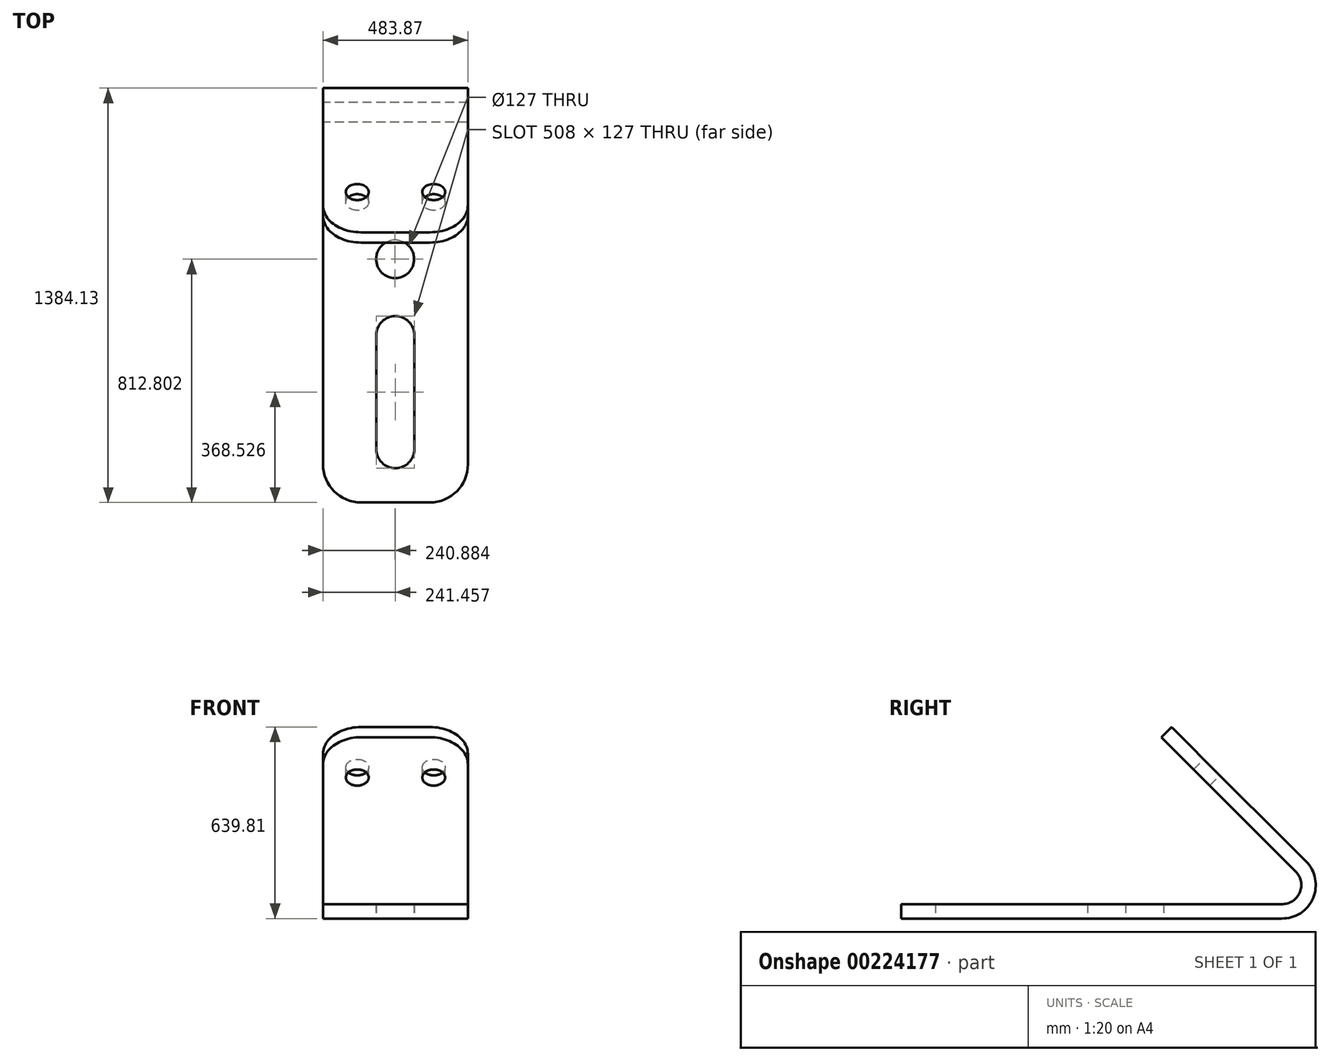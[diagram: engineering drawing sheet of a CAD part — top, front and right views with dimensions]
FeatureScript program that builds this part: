
annotation { "Feature Type Name" : "Feature", "Feature Type Description" : "" }
export const myFeature = defineFeature(function(context is Context, id is Id, definition is map)
    precondition{}
    {
        {
            var Q0;
            Q0=qCreatedBy(makeId("Top.planeOp"),FACE);
            var sketch = newSketch(context, id + "F0", { "sketchPlane" : qUnion([Q0])});
            skLineSegment(sketch, "E0.bottom", {"start": v(171.53, 635.71) * mm, "end": v(-312.34, 635.71) * mm});
            skLineSegment(sketch, "E0.top", {"start": v(171.53, -634.29) * mm, "end": v(-312.34, -634.29) * mm});
            skLineSegment(sketch, "E0.left", {"start": v(171.53, 635.71) * mm, "end": v(171.53, -634.29) * mm});
            skLineSegment(sketch, "E0.right", {"start": v(-312.34, 635.71) * mm, "end": v(-312.34, -634.29) * mm});
            skPoint(sketch, "E0.middle", {"position": v(-70.4, 0.71) * mm});
            skSolve(sketch);
        }
        {
            var Q0;
            Q0=makeQuery(id+"F0.imprint","IMPRINT",FACE,{"disambiguationData":[TD([[makeQuery(id+"F0.imprint","IMPRINT",EDGE,{"derivedFrom":sQuery(id+"F0.wireOp",EDGE,"E0.bottom")}),1.0]])]});
            extrude(context, id + "F1", {"entities" : qUnion([Q0]), "depth" : 48.26 * mm});
        }
        {
            var Q0;
            Q0=makeQuery(id+"F1.opExtrude","SWEPT_FACE",FACE,{"disambiguationData":[OSD([sQuery(id+"F0.wireOp",EDGE,"E0.right")])]});
            var sketch = newSketch(context, id + "F2", { "sketchPlane" : qUnion([Q0])});
            skArc(sketch, "E1", {"start": v(-635.71, 223.47) * mm, "mid": v(-749.84, 111.73) * mm, "end": v(-635.71, 0) * mm});
            skLineSegment(sketch, "E2", {"start": v(-749.84, 111.73) * mm, "end": v(-701.58, 111.73) * mm, "construction": true});
            skPoint(sketch, "E2.endSnap0", {"position": v(-749.84, 111.73) * mm});
            skArc(sketch, "E3", {"start": v(-635.71, 175.2) * mm, "mid": v(-701.58, 111.73) * mm, "end": v(-635.71, 48.26) * mm});
            skLineSegment(sketch, "E4", {"start": v(-717.1, 190.76) * mm, "end": v(-682.98, 156.65) * mm});
            skLineSegment(sketch, "E5", {"start": v(-717.1, 190.76) * mm, "end": v(-268.1, 639.78) * mm});
            skLineSegment(sketch, "E6", {"start": v(-682.98, 156.64) * mm, "end": v(-233.97, 605.66) * mm});
            skLineSegment(sketch, "E7", {"start": v(-268.1, 639.78) * mm, "end": v(-233.97, 605.66) * mm});
            skSolve(sketch);
        }
        {
            var Q0;
            {var subQ0=sQuery(id+"F2.wireOp",EDGE,"E4");Q0=makeQuery(id+"F2.imprint","IMPRINT",FACE,{"disambiguationData":[TD([[makeQuery(id+"F2.imprint","IMPRINT",EDGE,{"derivedFrom":subQ0}),1.0]])]});}
            var Q1;
            {var subQ3=sQuery(id+"F2.wireOp",EDGE,"E4");Q1=makeQuery(id+"F2.imprint","IMPRINT",FACE,{"disambiguationData":[TD([[makeQuery(id+"F2.imprint","IMPRINT",EDGE,{"derivedFrom":subQ3}),-1.0]])]});}
            extrude(context, id + "F3", {"entities" : qUnion([Q0, Q1]), "operationType" : NewBodyOperationType.ADD, "oppositeDirection" : true, "depth" : 483.87 * mm});
        }
        {
            var Q0;
            Q0=makeQuery(id+"F3.opExtrude","SWEPT_FACE",FACE,{"disambiguationData":[OSD([sQuery(id+"F2.wireOp",EDGE,"E5")])]});
            var sketch = newSketch(context, id + "F4", { "sketchPlane" : qUnion([Q0])});
            skLineSegment(sketch, "E8", {"start": v(312.34, 262.82) * mm, "end": v(312.34, 72.32) * mm, "construction": true});
            skLineSegment(sketch, "E9", {"start": v(312.34, 72.32) * mm, "end": v(198.04, 72.32) * mm, "construction": true});
            skLineSegment(sketch, "E10", {"start": v(-171.53, 72.32) * mm, "end": v(-57.23, 72.32) * mm, "construction": true});
            skCircle(sketch, "E11", {"center": v(-57.23, 72.32) * mm, "radius": 38.1 * mm});
            skCircle(sketch, "E12", {"center": v(198.04, 72.32) * mm, "radius": 38.1 * mm});
            skSolve(sketch);
        }
        {
            var Q0;
            Q0=makeQuery(id+"F4.imprint","IMPRINT",FACE,{"disambiguationData":[TD([[makeQuery(id+"F4.imprint","IMPRINT",EDGE,{"derivedFrom":sQuery(id+"F4.wireOp",EDGE,"E11")}),1.0]])]});
            var Q1;
            Q1=makeQuery(id+"F4.imprint","IMPRINT",FACE,{"disambiguationData":[TD([[makeQuery(id+"F4.imprint","IMPRINT",EDGE,{"derivedFrom":sQuery(id+"F4.wireOp",EDGE,"E12")}),1.0]])]});
            extrude(context, id + "F5", {"entities" : qUnion([Q0, Q1]), "operationType" : NewBodyOperationType.REMOVE, "oppositeDirection" : true, "depth" : 116.84 * mm});
        }
        {
            var Q0;
            Q0=makeQuery(id+"F3.opExtrude","CAP_EDGE",EDGE,{"disambiguationData":[OSD([sQuery(id+"F2.wireOp",EDGE,"E7")])],"isStart":false});
            var Q1;
            Q1=makeQuery(id+"F3.opExtrude","CAP_EDGE",EDGE,{"disambiguationData":[OSD([sQuery(id+"F2.wireOp",EDGE,"E7")])],"isStart":true});
            fillet(context, id + "F6", {"entities" : qUnion([Q0, Q1]), "radius" : 127 * mm, "tangentPropagation" : true, "allowEdgeOverflow" : false});
        }
        {
            var Q0;
            Q0=makeQuery(id+"F1.opExtrude","CAP_FACE",FACE,{"disambiguationData":[OSD([sQuery(id+"F0.wireOp",EDGE,"E0.bottom"),sQuery(id+"F0.wireOp",EDGE,"E0.top"),sQuery(id+"F0.wireOp",EDGE,"E0.left"),sQuery(id+"F0.wireOp",EDGE,"E0.right")])],"isStart":true});
            var sketch = newSketch(context, id + "F7", { "sketchPlane" : qUnion([Q0])});
            skCircle(sketch, "E13", {"center": v(-71.46, -178.51) * mm, "radius": 63.5 * mm});
            skLineSegment(sketch, "E14", {"start": v(-150.72, 519.99) * mm, "end": v(40.99, 519.99) * mm, "construction": true});
            skLineSegment(sketch, "E15", {"start": v(-70.4, 634.29) * mm, "end": v(-71.46, -178.51) * mm, "construction": true});
            skLineSegment(sketch, "E16.bottom", {"start": v(-7.38, 456.26) * mm, "end": v(-134.38, 456.26) * mm});
            skLineSegment(sketch, "E16.top", {"start": v(-7.38, 75.26) * mm, "end": v(-134.38, 75.26) * mm});
            skLineSegment(sketch, "E16.left", {"start": v(-7.38, 456.26) * mm, "end": v(-7.38, 75.26) * mm});
            skLineSegment(sketch, "E16.right", {"start": v(-134.38, 456.26) * mm, "end": v(-134.38, 75.26) * mm});
            skPoint(sketch, "E16.middle", {"position": v(-70.88, 265.76) * mm});
            skCircle(sketch, "E17", {"center": v(-70.88, 456.26) * mm, "radius": 63.5 * mm});
            skCircle(sketch, "E18", {"center": v(-70.88, 75.26) * mm, "radius": 63.5 * mm});
            skSolve(sketch);
        }
        {
            var Q0;
            {var subQ0=sQuery(id+"F7.wireOp",EDGE,"E16.bottom");Q0=makeQuery(id+"F7.imprint","IMPRINT",FACE,{"disambiguationData":[TD([[makeQuery(id+"F7.imprint","IMPRINT",EDGE,{"derivedFrom":subQ0}),1.0]])]});}
            var Q1;
            {var subQ0=sQuery(id+"F7.wireOp",EDGE,"E16.bottom");Q1=makeQuery(id+"F7.imprint","IMPRINT",FACE,{"disambiguationData":[TD([[makeQuery(id+"F7.imprint","IMPRINT",EDGE,{"derivedFrom":subQ0}),-1.0]])]});}
            var Q2;
            {var subQ0=sQuery(id+"F7.wireOp",EDGE,"E16.left");Q2=makeQuery(id+"F7.imprint","IMPRINT",FACE,{"disambiguationData":[TD([[makeQuery(id+"F7.imprint","IMPRINT",EDGE,{"derivedFrom":subQ0}),-1.0]])]});}
            var Q3;
            {var subQ0=sQuery(id+"F7.wireOp",EDGE,"E16.top");Q3=makeQuery(id+"F7.imprint","IMPRINT",FACE,{"disambiguationData":[TD([[makeQuery(id+"F7.imprint","IMPRINT",EDGE,{"derivedFrom":subQ0}),1.0]])]});}
            var Q4;
            {var subQ0=sQuery(id+"F7.wireOp",EDGE,"E16.top");Q4=makeQuery(id+"F7.imprint","IMPRINT",FACE,{"disambiguationData":[TD([[makeQuery(id+"F7.imprint","IMPRINT",EDGE,{"derivedFrom":subQ0}),-1.0]])]});}
            var Q5;
            Q5=makeQuery(id+"F7.imprint","IMPRINT",FACE,{"disambiguationData":[TD([[makeQuery(id+"F7.imprint","IMPRINT",EDGE,{"derivedFrom":sQuery(id+"F7.wireOp",EDGE,"E13")}),1.0]])]});
            extrude(context, id + "F8", {"entities" : qUnion([Q0, Q1, Q2, Q3, Q4, Q5]), "operationType" : NewBodyOperationType.REMOVE, "oppositeDirection" : true, "depth" : 200.66 * mm});
        }
        {
            var Q0;
            Q0=makeQuery(id+"F1.opExtrude","SWEPT_EDGE",EDGE,{"disambiguationData":[OSD([sQuery(id+"F0.wireOp",EDGE,"E0.top"),sQuery(id+"F0.wireOp",EDGE,"E0.right")])]});
            fillet(context, id + "F9", {"entities" : qUnion([Q0]), "radius" : 127 * mm, "tangentPropagation" : true, "allowEdgeOverflow" : false});
        }
        {
            var Q0;
            Q0=makeQuery(id+"F1.opExtrude","SWEPT_EDGE",EDGE,{"disambiguationData":[OSD([sQuery(id+"F0.wireOp",EDGE,"E0.top"),sQuery(id+"F0.wireOp",EDGE,"E0.left")])]});
            fillet(context, id + "F10", {"entities" : qUnion([Q0]), "radius" : 127 * mm, "tangentPropagation" : true, "allowEdgeOverflow" : false});
        }
    });
